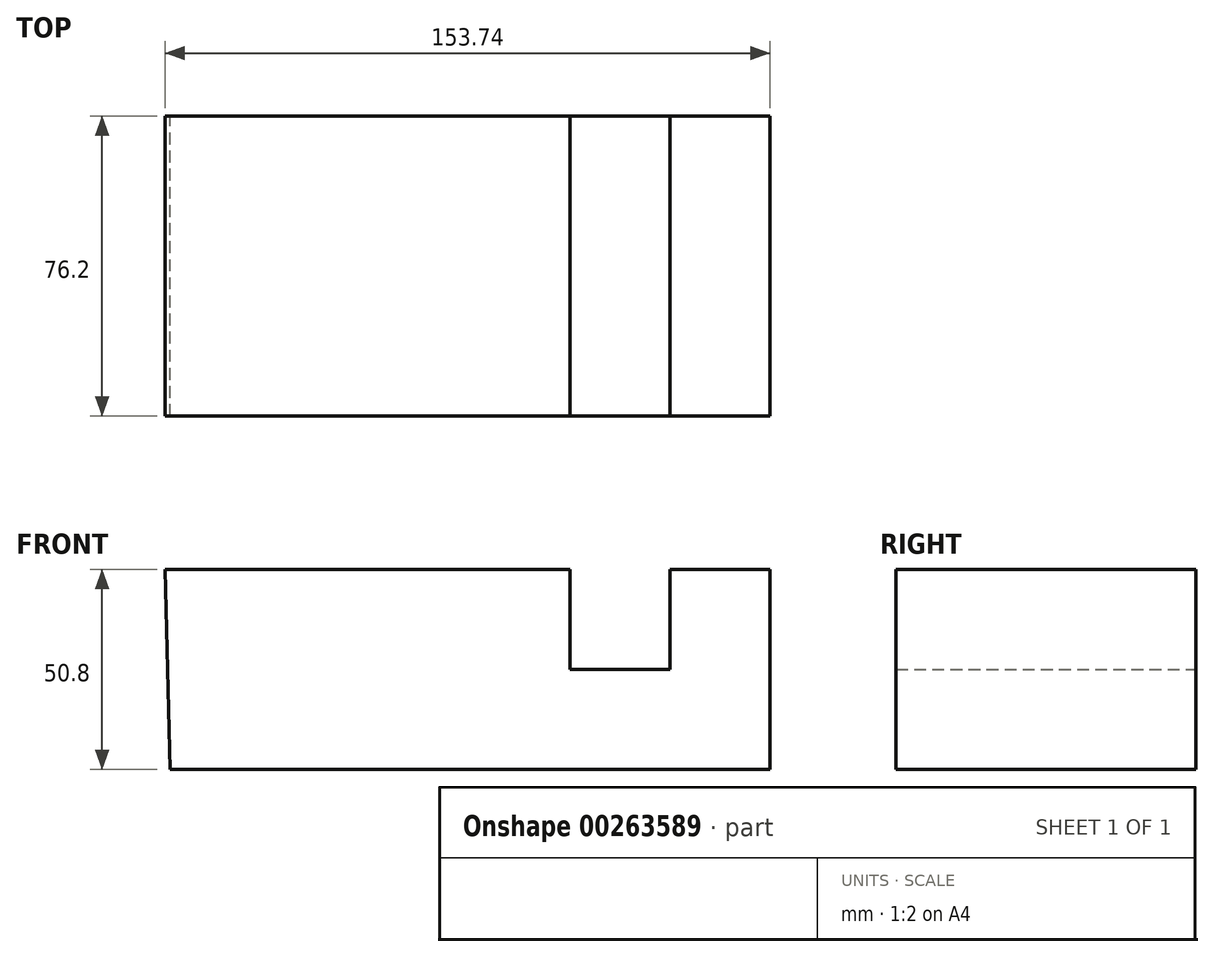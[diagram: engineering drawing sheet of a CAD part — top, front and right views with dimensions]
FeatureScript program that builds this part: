
annotation { "Feature Type Name" : "Feature", "Feature Type Description" : "" }
export const myFeature = defineFeature(function(context is Context, id is Id, definition is map)
    precondition{}
    {
        {
            var Q0;
            Q0=qCreatedBy(makeId("Front.planeOp"),FACE);
            var sketch = newSketch(context, id + "F0", { "sketchPlane" : qUnion([Q0])});
            skLineSegment(sketch, "E0", {"start": v(-76, 0) * mm, "end": v(76.4, 0) * mm});
            skLineSegment(sketch, "E1", {"start": v(76.4, 0) * mm, "end": v(76.4, 50.8) * mm});
            skLineSegment(sketch, "E2", {"start": v(76.4, 50.8) * mm, "end": v(51, 50.8) * mm});
            skLineSegment(sketch, "E3", {"start": v(51, 50.8) * mm, "end": v(51, 25.4) * mm});
            skLineSegment(sketch, "E4", {"start": v(51, 25.4) * mm, "end": v(25.6, 25.4) * mm});
            skLineSegment(sketch, "E5", {"start": v(25.6, 25.4) * mm, "end": v(25.6, 50.8) * mm});
            skLineSegment(sketch, "E6", {"start": v(25.6, 50.8) * mm, "end": v(-77.34, 50.8) * mm});
            skLineSegment(sketch, "E7", {"start": v(-77.34, 50.8) * mm, "end": v(-76, 0) * mm});
            skSolve(sketch);
        }
        {
            var Q0;
            Q0=makeQuery(id+"F0.imprint","IMPRINT",FACE,{"disambiguationData":[TD([[makeQuery(id+"F0.imprint","IMPRINT",EDGE,{"derivedFrom":sQuery(id+"F0.wireOp",EDGE,"E0")}),1.0]])]});
            extrude(context, id + "F1", {"entities" : qUnion([Q0]), "depth" : 76.2 * mm});
        }
    });
